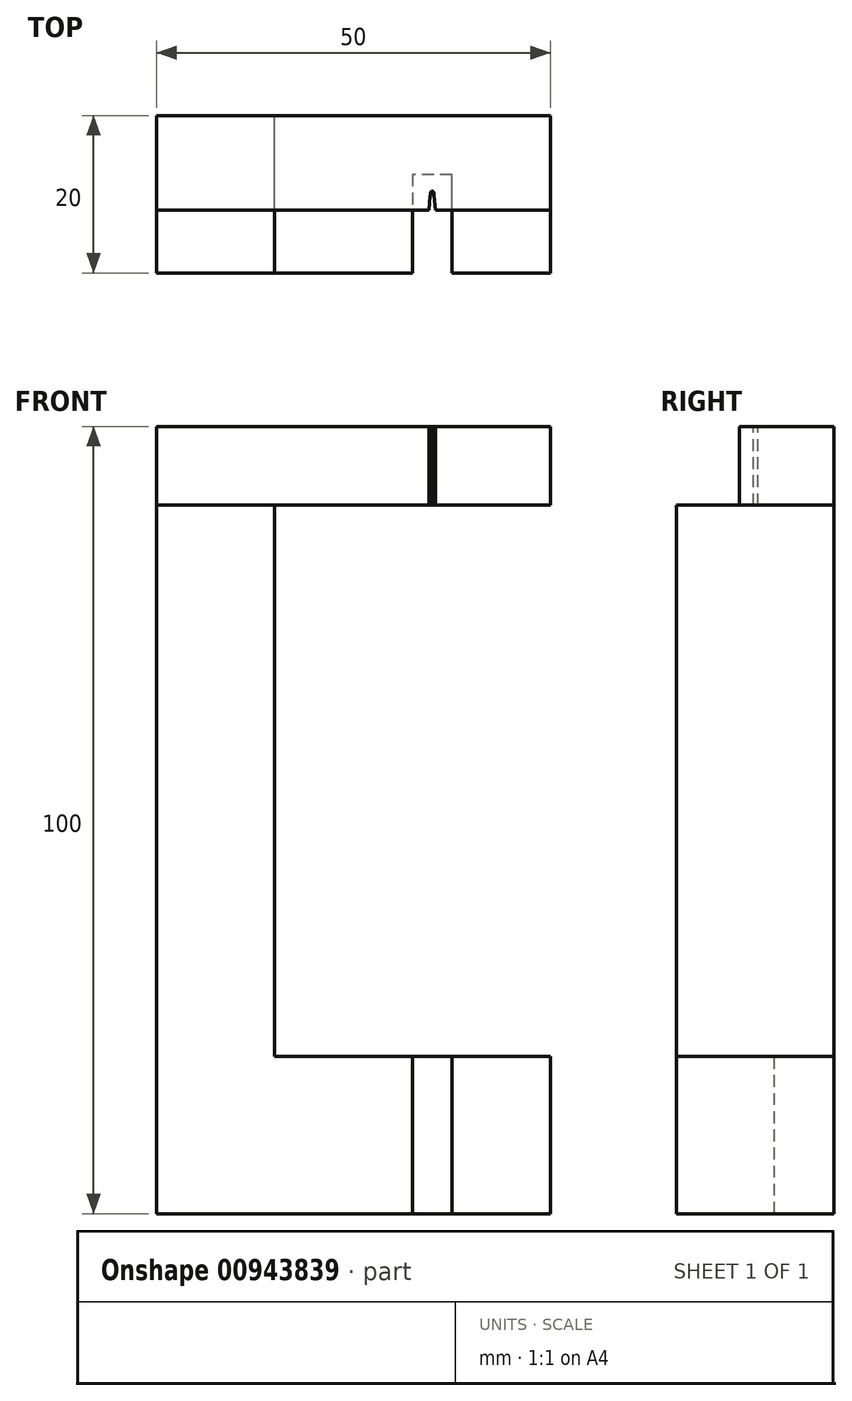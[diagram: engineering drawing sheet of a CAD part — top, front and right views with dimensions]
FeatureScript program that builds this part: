
annotation { "Feature Type Name" : "Feature", "Feature Type Description" : "" }
export const myFeature = defineFeature(function(context is Context, id is Id, definition is map)
    precondition{}
    {
        {
            var Q0;
            Q0=qCreatedBy(makeId("Front.planeOp"),FACE);
            var sketch = newSketch(context, id + "F0", { "sketchPlane" : qUnion([Q0])});
            skLineSegment(sketch, "E0.bottom", {"start": v(25, -10) * mm, "end": v(-25, -10) * mm});
            skLineSegment(sketch, "E0.top", {"start": v(25, 10) * mm, "end": v(-10, 10) * mm});
            skLineSegment(sketch, "E0.left", {"start": v(25, -10) * mm, "end": v(25, 10) * mm});
            skLineSegment(sketch, "E0.right", {"start": v(-25, -10) * mm, "end": v(-25, 10) * mm});
            skPoint(sketch, "E0.middle", {"position": v(0, 0) * mm});
            skLineSegment(sketch, "E1.top", {"start": v(-25, 90) * mm, "end": v(-10, 90) * mm});
            skLineSegment(sketch, "E1.left", {"start": v(-25, 10) * mm, "end": v(-25, 90) * mm});
            skLineSegment(sketch, "E1.right", {"start": v(-10, 10) * mm, "end": v(-10, 80) * mm});
            skPoint(sketch, "E1.middle", {"position": v(-17.5, 50) * mm});
            skLineSegment(sketch, "E2.bottom", {"start": v(-10, 90) * mm, "end": v(25, 90) * mm});
            skLineSegment(sketch, "E2.top", {"start": v(-10, 80) * mm, "end": v(25, 80) * mm});
            skLineSegment(sketch, "E2.right", {"start": v(25, 90) * mm, "end": v(25, 80) * mm});
            skSolve(sketch);
        }
        {
            var Q0;
            Q0 = qSketchRegion(id + "F0", true);
            extrude(context, id + "F1", {"entities" : qUnion([Q0]), "depth" : 20 * mm, "offsetDistance" : 25 * mm});
        }
        {
            var Q0;
            Q0=makeQuery(id+"F1.opExtrude","SWEPT_FACE",FACE,{"disambiguationData":[OSD([sQuery(id+"F0.wireOp",EDGE,"E0.top")])]});
            var sketch = newSketch(context, id + "F2", { "sketchPlane" : qUnion([Q0])});
            skLineSegment(sketch, "E3.bottom", {"start": v(12.5, -7.5) * mm, "end": v(7.5, -7.5) * mm});
            skLineSegment(sketch, "E3.left", {"start": v(12.5, -7.5) * mm, "end": v(12.5, -12.5) * mm});
            skLineSegment(sketch, "E3.right", {"start": v(7.5, -7.5) * mm, "end": v(7.5, -12.5) * mm});
            skPoint(sketch, "E3.middle", {"position": v(10, -10) * mm});
            skPoint(sketch, "E3.middle.positionSnap0", {"position": v(25, -10) * mm});
            skPoint(sketch, "E3.centerSnap0", {"position": v(25, -10) * mm});
            skLineSegment(sketch, "E4", {"start": v(7.5, -12.5) * mm, "end": v(7.5, -20) * mm});
            skLineSegment(sketch, "E5", {"start": v(7.5, -20) * mm, "end": v(12.5, -20) * mm});
            skLineSegment(sketch, "E6", {"start": v(12.5, -20) * mm, "end": v(12.5, -12.5) * mm});
            skSolve(sketch);
        }
        {
            var Q0;
            Q0 = qSketchRegion(id + "F2", true);
            extrude(context, id + "F3", {"entities" : qUnion([Q0]), "operationType" : NewBodyOperationType.REMOVE, "oppositeDirection" : true, "depth" : 20 * mm, "offsetDistance" : 25 * mm});
        }
        {
            var Q0;
            Q0=makeQuery(id+"F1.opExtrude","SWEPT_FACE",FACE,{"disambiguationData":[OSD([sQuery(id+"F0.wireOp",EDGE,"E1.top"),sQuery(id+"F0.wireOp",EDGE,"E2.bottom")])]});
            var sketch = newSketch(context, id + "F4", { "sketchPlane" : qUnion([Q0])});
            skLineSegment(sketch, "E7.left", {"start": v(10.2, -10.2) * mm, "end": v(10.2, -9.8) * mm});
            skLineSegment(sketch, "E7.right", {"start": v(9.8, -10.2) * mm, "end": v(9.8, -9.8) * mm});
            skPoint(sketch, "E7.middle", {"position": v(10, -10) * mm});
            skPoint(sketch, "E7.middle.positionSnap0", {"position": v(25, -10) * mm});
            skPoint(sketch, "E7.centerSnap0", {"position": v(25, -10) * mm});
            skArc(sketch, "E8", {"start": v(10.2, -9.8) * mm, "mid": v(10, -9.6) * mm, "end": v(9.8, -9.8) * mm});
            skArc(sketch, "E9", {"start": v(9.8, -10.2) * mm, "mid": v(10, -10.4) * mm, "end": v(10.2, -10.2) * mm});
            skSolve(sketch);
        }
        {
            var Q0;
            Q0 = qSketchRegion(id + "F4", true);
            extrude(context, id + "F5", {"entities" : qUnion([Q0]), "operationType" : NewBodyOperationType.REMOVE, "oppositeDirection" : true, "depth" : 25 * mm, "offsetDistance" : 25 * mm});
        }
        {
            var Q0;
            Q0=makeQuery(id+"F1.opExtrude","SWEPT_FACE",FACE,{"disambiguationData":[OSD([sQuery(id+"F0.wireOp",EDGE,"E1.top"),sQuery(id+"F0.wireOp",EDGE,"E2.bottom")])]});
            var sketch = newSketch(context, id + "F6", { "sketchPlane" : qUnion([Q0])});
            skLineSegment(sketch, "E10", {"start": v(25, -12) * mm, "end": v(10.4, -12) * mm});
            skLineSegment(sketch, "E11", {"start": v(9.8, -10.2) * mm, "end": v(9.75, -10.2) * mm});
            skLineSegment(sketch, "E12", {"start": v(9.75, -10.2) * mm, "end": v(9.6, -12) * mm});
            skLineSegment(sketch, "E13", {"start": v(10.2, -10.2) * mm, "end": v(10.25, -10.2) * mm});
            skLineSegment(sketch, "E14", {"start": v(10.25, -10.2) * mm, "end": v(10.4, -12) * mm});
            skLineSegment(sketch, "E15.trimOffspring", {"start": v(9.6, -12) * mm, "end": v(-25, -12) * mm});
            skPoint(sketch, "E16.start.orphan", {"position": v(25, -10) * mm});
            skLineSegment(sketch, "E17", {"start": v(-25, -12) * mm, "end": v(-25, -20) * mm});
            skLineSegment(sketch, "E18", {"start": v(-25, -20) * mm, "end": v(25, -20) * mm});
            skLineSegment(sketch, "E19", {"start": v(25, -20) * mm, "end": v(25, -12) * mm});
            skLineSegment(sketch, "E20", {"start": v(9.8, -10.2) * mm, "end": v(10.2, -10.2) * mm});
            skSolve(sketch);
        }
        {
            var Q0;
            Q0 = qSketchRegion(id + "F6", true);
            extrude(context, id + "F7", {"entities" : qUnion([Q0]), "operationType" : NewBodyOperationType.REMOVE, "oppositeDirection" : true, "depth" : 10 * mm, "offsetDistance" : 25 * mm});
        }
    });
